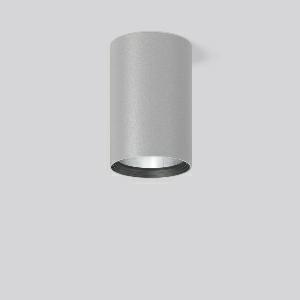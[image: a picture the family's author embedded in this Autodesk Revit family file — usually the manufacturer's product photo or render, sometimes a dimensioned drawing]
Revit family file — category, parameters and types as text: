
# Revit family: heledon_maxi_a_931231_004_76_e4d7
name_source: partatom
category: Lighting Fixtures
units: mm (PartAtom-declared; Revit-internal decimal feet)

## family parameters
Cut with Voids When Loaded = No
Host = Face
Light Source = No
Part Type = Normal
Room Calculation Point = No
Round Connector Dimension = Use Diameter
Shared = No

## types (1)
- HELEDON maxi A (1 x LED Modul 932 fresh meat, 2150 lm, 3200)
    Apparent Load = 33 VA
    Approval mark = CE
    CIE Flux Codes = 100 100 100 100 100
    Color Rendering = 90
    Color Temperature = 3200
    Default Elevation = 1800 mm
    Description = Series: HELEDON maxi
Cylindrical surface-mounted downlight. Housing: die-cast aluminium, powder-coated. Internal ceiling frame polycarbonate with bayonet mounting. Black plastic ring and recessed LED to prevent glare from the side. Optical assembly with reflector made of MIRO-Silver with 98% total light reflection for outstanding efficiency - can be changed without tools. Special LED for illumination of meat included. Suitable for Ceiling mounting. Easy installation with a separate ceiling frame with bayonet mounting and plug connection. Driver integrated. Connected via plug-in connector. High quality converter without flickering and stroboscopic effect. The following accessories can be mounted without use of tools: interchangeable lenses, decorative glasses, honeycomb louvre, clear and frosted diffusers, white interchangeable plastic ring. 
Colour: silver
Diameter: 123 mm
Height: 183 mm
Lamp: LED
Socket: without socket
Colour temperature: fresh meat
System power: 33 W
Rated luminous flux: 2150 lm
Luminous efficiency: 65 lm/W
Control gear: Converter, dimmable, DALI
Protection class: I
Type of protection: IP 20
    Height = 183 mm
    Lamp = 1 x LED Modul 932 fresh meat
    Lamp Light Flux = 2150 lm
    Lamp count = 1
    Length = 123 mm
    Lifetime = 50000 h
    Luminous efficacy = 65 lm/W
    Manufacturer = RZB
    ModVariant = No
    Model = 931231.004.76
    Mounting Place = Ceiling
    Mounting Type = Surface mounted
    Number of Poles = 1
    OnlyDefault = Yes
    Power Factor = 1
    Product Name = HELEDON maxi A
    Product group = Surface mounted downlights
    ProductGroupID = 302
    Protection Class = Protection class I
    Protection Degree = IP 20
    RLX_Detail_Level = 1
    RLX_Emergency_Light_Flux = 0 lm
    RLX_Emergency_Type = 0
    RLX_Emergency_Type_DB = No
    RlxData = <blob elided: 99405 chars, md5=ce0f37c8>
    Socket = socket
    Standby Power = 0 W
    System Light Flux = 2150 lm
    System Power = 33 W
    Type Comments = Product without accessories
    Type Image = 931192.004.jpg
    URL = http://relux.com
    VarID = ---
    Voltage = 230 V
    Voltage Range = 220-240 V
    Weight = 0.00 kg
    Width = 0 mm  [stored 0 ft]

note: [stored X ft] marks values corroborated as IEEE doubles in the binary element streams (Revit-internal decimal feet)

## geometry (parser evidence)
native form markers: Blend x4, Sweep x10
no freeform markers — native parametric forms only
